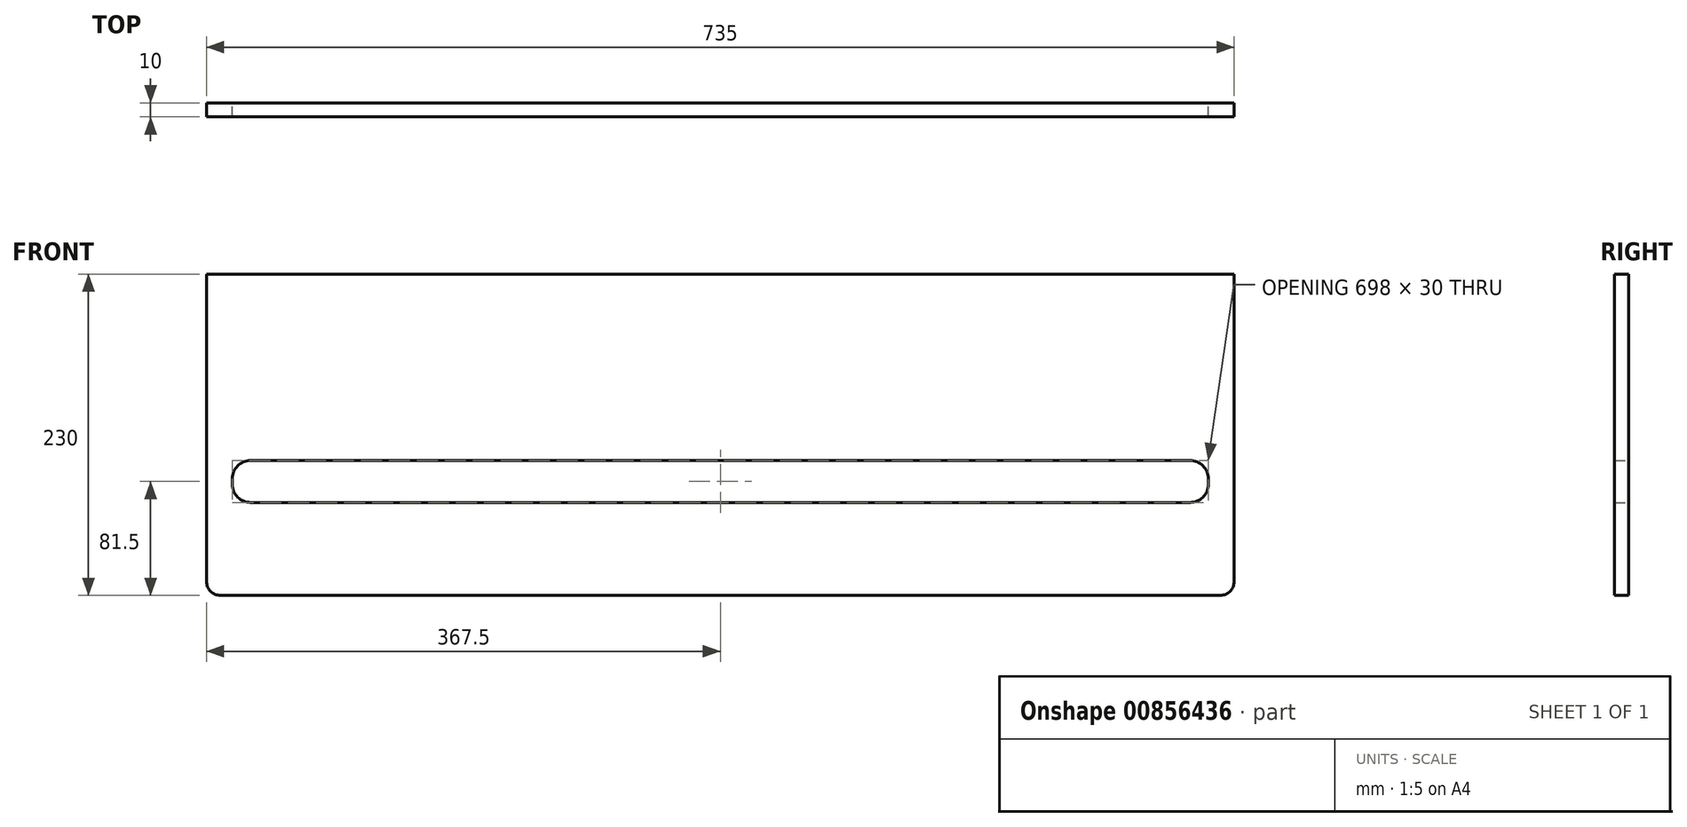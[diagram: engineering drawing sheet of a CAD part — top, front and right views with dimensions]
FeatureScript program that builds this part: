
annotation { "Feature Type Name" : "Feature", "Feature Type Description" : "" }
export const myFeature = defineFeature(function(context is Context, id is Id, definition is map)
    precondition{}
    {
        {
            var Q0;
            Q0=qCreatedBy(makeId("Front.planeOp"),FACE);
            var sketch = newSketch(context, id + "F0", { "sketchPlane" : qUnion([Q0])});
            skLineSegment(sketch, "E0.bottom", {"start": v(10, 0) * mm, "end": v(725, 0) * mm});
            skLineSegment(sketch, "E0.top", {"start": v(0, 230) * mm, "end": v(735, 230) * mm});
            skLineSegment(sketch, "E0.left", {"start": v(0, 10) * mm, "end": v(0, 230) * mm});
            skLineSegment(sketch, "E0.right", {"start": v(735, 10) * mm, "end": v(735, 230) * mm});
            skLineSegment(sketch, "E1.bottom", {"start": v(31.5, 96.5) * mm, "end": v(703.5, 96.5) * mm});
            skLineSegment(sketch, "E1.top", {"start": v(31.5, 66.5) * mm, "end": v(703.5, 66.5) * mm});
            skLineSegment(sketch, "E1.left", {"start": v(18.5, 83.5) * mm, "end": v(18.5, 79.5) * mm});
            skLineSegment(sketch, "E1.right", {"start": v(716.5, 83.5) * mm, "end": v(716.5, 79.5) * mm});
            skPoint(sketch, "E2.visualSharp", {"position": v(18.5, 96.5) * mm});
            skArc(sketch, "E2.filletArc", {"start": v(31.5, 96.5) * mm, "mid": v(22.3, 92.7) * mm, "end": v(18.5, 83.5) * mm});
            skPoint(sketch, "E3.visualSharp", {"position": v(18.5, 66.5) * mm});
            skArc(sketch, "E3.filletArc", {"start": v(18.5, 79.5) * mm, "mid": v(22.3, 70.3) * mm, "end": v(31.5, 66.5) * mm});
            skPoint(sketch, "E4.visualSharp", {"position": v(716.5, 96.5) * mm});
            skArc(sketch, "E4.filletArc", {"start": v(716.5, 83.5) * mm, "mid": v(712.7, 92.7) * mm, "end": v(703.5, 96.5) * mm});
            skPoint(sketch, "E5.visualSharp", {"position": v(716.5, 66.5) * mm});
            skArc(sketch, "E5.filletArc", {"start": v(703.5, 66.5) * mm, "mid": v(712.7, 70.3) * mm, "end": v(716.5, 79.5) * mm});
            skPoint(sketch, "E6.0.visualSharp", {"position": v(0, 0) * mm});
            skArc(sketch, "E6.0.filletArc", {"start": v(0, 10) * mm, "mid": v(2.93, 2.93) * mm, "end": v(10, 0) * mm});
            skPoint(sketch, "E6.1.visualSharp", {"position": v(735, 0) * mm});
            skArc(sketch, "E6.1.filletArc", {"start": v(725, 0) * mm, "mid": v(732.07, 2.93) * mm, "end": v(735, 10) * mm});
            skSolve(sketch);
        }
        {
            var Q0;
            Q0=makeQuery(id+"F0.imprint","IMPRINT",FACE,{"disambiguationData":[TD([[makeQuery(id+"F0.imprint","IMPRINT",EDGE,{"derivedFrom":sQuery(id+"F0.wireOp",EDGE,"E0.bottom")}),1.0]])]});
            extrude(context, id + "F1", {"entities" : qUnion([Q0]), "flatOperationType" : FlatOperationType.REMOVE, "depth" : 10 * mm, "offsetDistance" : 25 * mm, "domain" : OperationDomain.MODEL});
        }
    });
